# Revit family: Sanitary_Taps&Mixers_Zurn_Z812B4-XL
name_source: partatom
category: Plumbing Fixtures
units: mm (PartAtom-declared; Revit-internal decimal feet)

## family parameters
Cut with Voids When Loaded = No
Host = Face
Maintain Annotation Orientation = No
OmniClass Number = 23.45.55.17
OmniClass Title = Mixing Faucets
Part Type = Normal
Room Calculation Point = No
Round Connector Dimension = Use Radius
Shared = No

## types (13) — shared parameters
ADA Compliance = Yes
Assembly Code = D2010.60
CW Connection = Yes
CWFU = 1
Default Elevation = 48 "
Description = 4 in CENTERSET GOOSENECK FAUCET
Distance B/W Base & Aerator = 8 "
Distance Between Centerset = 4 "
HW Connection = Yes
HWFU = 1
Inlet Connection Size (inch) = 1 "
Lead- Free Compliant = Yes
Main Material = Brass_Zurn_ Chrome Polished
Manufacturer = Zurn Water, LLC
Manufacturer Brand = Zurn
Model = Z812B4-XL
Modified Date = 03/17/2026
Product Documentation Link = https://files.zurn.com
Product Installation Sheet URL = https://files.zurn.com
Product Page URL = https://www.zurn.com
Product data URL = https://bimobject.com
Spout Base Width = 6 "
Spout Reach = 5.375 "
URL = https://www.zurn.com
Vent Connection = No
Waste Connection = No
Width of Handle = 4 "
zero-valued in all types: WFU

## per-type parameters (varying)
| type | AERATOR | Flow Rate | Type of Outlet | Water Sense Compliance |
| Z812B4-XL-16F (1.0 GPM SPRAY OUTLET) | Yes | 1 GPM | SPRAY | No |
| Z812B4-XL-17F (1.5 GPM AERATOR OUTLET) | Yes | 2 GPM | AERATOR | Yes |
| Z812B4-XL-18F (1.5 GPM LAMINAR OUTLET) | Yes | 2 GPM | LAMINAR | Yes |
| Z812B4-XL-22F (1.0 GPM LAMINAR OUTLET) | Yes | 1 GPM | LAMINAR | No |
| Z812B4-XL-28F (0.5 GPM LAMINAR OUTLET) | Yes | 1 GPM | LAMINAR | No |
| Z812B4-XL-3F (0.5 GPM SPRAY OUTLET) | Yes | 1 GPM | SPRAY | No |
| Z812B4-XL-4F (2.2 GPM LAMINAR OUTLET) | Yes | 2 GPM | LAMINAR | No |
| Z812B4-XL-7F (1.0 GPM SPRAY OUTLET) | Yes | 1 GPM | SPRAY | Yes |
| Z812B4-XL-2F (2.2 GPM AREATOR OUTLET) | Yes | 2 GPM | AERATOR | No |
| Z812B4-XL-FC0.5 (0.5 GPM LAMINAR OUTLET) -FLOW CONTROL | No | 1 GPM | LAMINAR | No |
| Z812B4-XL-FC1.0 (1.0 GPM LAMINAR OUTLET) -FLOW CONTROL | No | 1 GPM | LAMINAR | Yes |
| Z812B4-XL-FC1.5 (1.5 GPM LAMINAR OUTLET) -FLOW CONTROL | No | 2 GPM | LAMINAR | Yes |
| Z812B4-XL-FC (2.0 GPM LAMINAR OUTLET) -FLOW CONTROL | No | 2 GPM | LAMINAR | No |

## geometry (parser evidence)
native form markers: Sweep x23
no freeform markers — native parametric forms only
